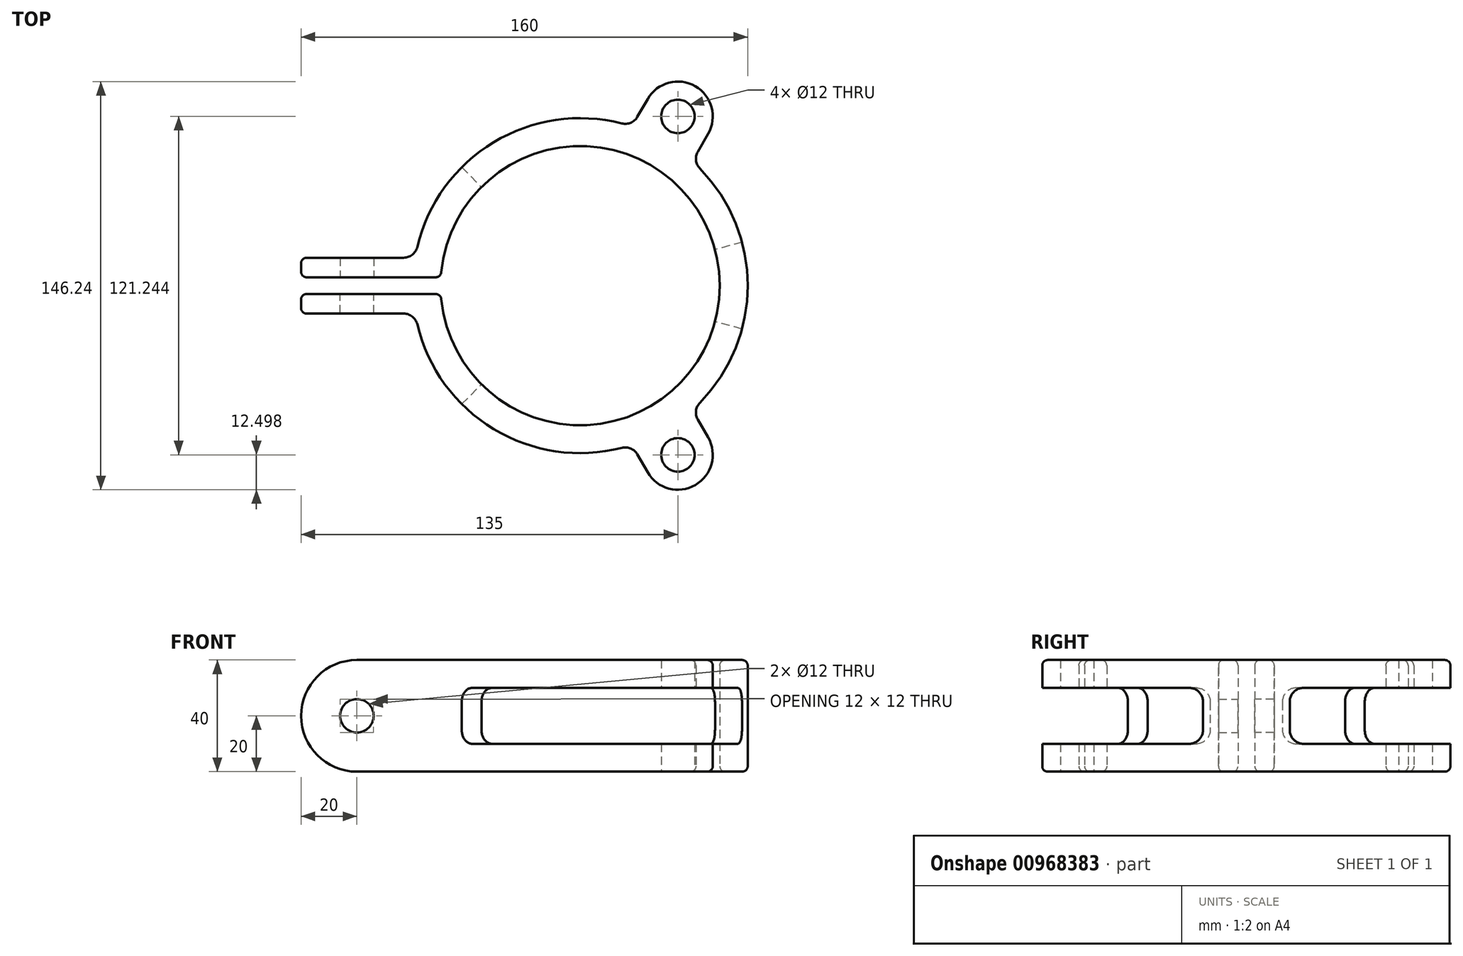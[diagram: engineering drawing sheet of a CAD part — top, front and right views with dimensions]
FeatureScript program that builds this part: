
annotation { "Feature Type Name" : "Feature", "Feature Type Description" : "" }
export const myFeature = defineFeature(function(context is Context, id is Id, definition is map)
    precondition{}
    {
        {
            var Q0;
            Q0=qCreatedBy(makeId("Top.planeOp"),FACE);
            var sketch = newSketch(context, id + "F0", { "sketchPlane" : qUnion([Q0])});
            skArc(sketch, "E0", {"start": v(50, 0) * mm, "mid": v(2.4, 49.94) * mm, "end": v(-49.77, 4.8) * mm});
            skArc(sketch, "E1", {"start": v(14.9, 58.12) * mm, "mid": v(-31.03, 51.36) * mm, "end": v(-58.38, 13.85) * mm});
            skLineSegment(sketch, "E2", {"start": v(-51.76, 3) * mm, "end": v(-100, 3) * mm});
            skLineSegment(sketch, "E3", {"start": v(-100, 3) * mm, "end": v(-100, 10) * mm});
            skLineSegment(sketch, "E4", {"start": v(-100, 10) * mm, "end": v(-63.25, 10) * mm});
            skLineSegment(sketch, "E5", {"start": v(50, 0) * mm, "end": v(60, 0) * mm});
            skArc(sketch, "E6", {"start": v(45.22, 53.43) * mm, "mid": v(41.25, 71.45) * mm, "end": v(23.66, 65.88) * mm});
            skCircle(sketch, "E7", {"center": v(35, 60.62) * mm, "radius": 6 * mm});
            skLineSegment(sketch, "E8", {"start": v(35, 60.62) * mm, "end": v(0, 0) * mm, "construction": true});
            skArc(sketch, "E9", {"start": v(70, 0) * mm, "mid": v(0, 70) * mm, "end": v(-70, 0) * mm, "construction": true});
            skLineSegment(sketch, "E10", {"start": v(24.17, 66.87) * mm, "end": v(20.47, 60.46) * mm});
            skLineSegment(sketch, "E11", {"start": v(45.83, 54.37) * mm, "end": v(42.13, 47.96) * mm});
            skPoint(sketch, "E12.newPointA", {"position": v(60, 0) * mm});
            skArc(sketch, "E12.filletArc", {"start": v(14.9, 58.12) * mm, "mid": v(18.08, 58.35) * mm, "end": v(20.47, 60.46) * mm});
            skArc(sketch, "E13", {"start": v(60, 0) * mm, "mid": v(55.56, 22.66) * mm, "end": v(42.88, 41.97) * mm});
            skArc(sketch, "E14.filletArc", {"start": v(42.13, 47.96) * mm, "mid": v(41.5, 44.84) * mm, "end": v(42.88, 41.97) * mm});
            skPoint(sketch, "E15.visualSharp", {"position": v(-59.16, 10) * mm});
            skArc(sketch, "E15.filletArc", {"start": v(-63.25, 10) * mm, "mid": v(-60.14, 11.08) * mm, "end": v(-58.38, 13.85) * mm});
            skPoint(sketch, "E16.visualSharp", {"position": v(-49.9, 3) * mm});
            skArc(sketch, "E16.filletArc", {"start": v(-51.76, 3) * mm, "mid": v(-50.41, 3.52) * mm, "end": v(-49.77, 4.8) * mm});
            skPoint(sketch, "E17.visualSharp", {"position": v(-100, 10) * mm});
            skPoint(sketch, "E18.visualSharp", {"position": v(-100, 3) * mm});
            skSolve(sketch);
        }
        {
            var Q0;
            Q0=makeQuery(id+"F0.imprint","IMPRINT",FACE,{"disambiguationData":[TD([[makeQuery(id+"F0.imprint","IMPRINT",EDGE,{"derivedFrom":sQuery(id+"F0.wireOp",EDGE,"E0")}),-1.0]])]});
            extrude(context, id + "F1", {"entities" : qUnion([Q0]), "depth" : 40 * mm, "offsetDistance" : 25 * mm, "symmetric" : true});
        }
        {
            var Q0;
            Q0=makeQuery(id+"F1.opExtrude","CAP_EDGE",EDGE,{"disambiguationData":[OSD([sQuery(id+"F0.wireOp",EDGE,"E3")])],"isStart":false});
            var Q1;
            Q1=makeQuery(id+"F1.opExtrude","CAP_EDGE",EDGE,{"disambiguationData":[OSD([sQuery(id+"F0.wireOp",EDGE,"E3")])],"isStart":true});
            fillet(context, id + "F2", {"entities" : qUnion([Q0, Q1]), "radius" : 20 * mm, "tangentPropagation" : true, "allowEdgeOverflow" : false});
        }
        {
            var Q0;
            Q0=qCreatedBy(makeId("Front.planeOp"),FACE);
            var sketch = newSketch(context, id + "F3", { "sketchPlane" : qUnion([Q0])});
            skCircle(sketch, "E19", {"center": v(-80, 0) * mm, "radius": 6 * mm});
            skSolve(sketch);
        }
        {
            var Q0;
            Q0=makeQuery(id+"F3.imprint","IMPRINT",FACE,{"disambiguationData":[TD([[makeQuery(id+"F3.imprint","IMPRINT",EDGE,{"derivedFrom":sQuery(id+"F3.wireOp",EDGE,"E19")}),1.0]])]});
            extrude(context, id + "F4", {"entities" : qUnion([Q0]), "operationType" : NewBodyOperationType.REMOVE, "endBound" : BoundingType.THROUGH_ALL, "oppositeDirection" : true, "depth" : 25 * mm, "offsetDistance" : 25 * mm});
        }
        {
            var Q0;
            Q0=qCreatedBy(makeId("Top.planeOp"),FACE);
            var sketch = newSketch(context, id + "F5", { "sketchPlane" : qUnion([Q0])});
            skArc(sketch, "E20.0", {"start": v(14.9, 58.12) * mm, "mid": v(-15.84, 57.87) * mm, "end": v(-42.43, 42.43) * mm});
            skArc(sketch, "E20.1", {"start": v(48.3, 12.94) * mm, "mid": v(12.94, 48.3) * mm, "end": v(-35.36, 35.36) * mm});
            skLineSegment(sketch, "E21", {"start": v(-42.43, 42.43) * mm, "end": v(-35.36, 35.36) * mm});
            skPoint(sketch, "E22.orphan", {"position": v(14.9, 58.12) * mm});
            skLineSegment(sketch, "E23", {"start": v(57.96, 15.53) * mm, "end": v(48.3, 12.94) * mm});
            skPoint(sketch, "E24.orphan", {"position": v(50, 0) * mm});
            skPoint(sketch, "E25.orphan", {"position": v(-49.77, 4.8) * mm});
            skPoint(sketch, "E26.orphan", {"position": v(-58.38, 13.85) * mm});
            skArc(sketch, "E27.0", {"start": v(57.96, 15.53) * mm, "mid": v(52.12, 29.72) * mm, "end": v(42.88, 41.97) * mm});
            skArc(sketch, "E27.1", {"start": v(42.13, 47.96) * mm, "mid": v(41.5, 44.84) * mm, "end": v(42.88, 41.97) * mm});
            skLineSegment(sketch, "E27.2", {"start": v(45.83, 54.37) * mm, "end": v(42.13, 47.96) * mm});
            skArc(sketch, "E27.3", {"start": v(45.22, 53.43) * mm, "mid": v(41.25, 71.45) * mm, "end": v(23.66, 65.88) * mm});
            skLineSegment(sketch, "E27.4", {"start": v(24.17, 66.87) * mm, "end": v(20.47, 60.46) * mm});
            skArc(sketch, "E27.5", {"start": v(14.9, 58.12) * mm, "mid": v(18.08, 58.35) * mm, "end": v(20.47, 60.46) * mm});
            skPoint(sketch, "E28.orphan", {"position": v(60, 0) * mm});
            skSolve(sketch);
        }
        {
            var Q0;
            Q0 = qSketchRegion(id + "F5", true);
            extrude(context, id + "F6", {"entities" : qUnion([Q0]), "operationType" : NewBodyOperationType.REMOVE, "depth" : 20 * mm, "offsetDistance" : 25 * mm, "symmetric" : true});
        }
        {
            var Q0;
            Q0=makeQuery(id+"F6.boolean.opBoolean","COPY",EDGE,{"derivedFrom":makeQuery(id+"F6.opExtrude","CAP_EDGE",EDGE,{"disambiguationData":[OSD([sQuery(id+"F5.wireOp",EDGE,"E21")])],"isStart":true})});
            var Q1;
            Q1=makeQuery(id+"F6.boolean.opBoolean","COPY",EDGE,{"derivedFrom":makeQuery(id+"F6.opExtrude","CAP_EDGE",EDGE,{"disambiguationData":[OSD([sQuery(id+"F5.wireOp",EDGE,"E21")])],"isStart":false})});
            var Q2;
            Q2=makeQuery(id+"F6.boolean.opBoolean","COPY",EDGE,{"derivedFrom":makeQuery(id+"F6.opExtrude","CAP_EDGE",EDGE,{"disambiguationData":[OSD([sQuery(id+"F5.wireOp",EDGE,"E23")])],"isStart":false})});
            var Q3;
            Q3=makeQuery(id+"F6.boolean.opBoolean","COPY",EDGE,{"derivedFrom":makeQuery(id+"F6.opExtrude","CAP_EDGE",EDGE,{"disambiguationData":[OSD([sQuery(id+"F5.wireOp",EDGE,"E23")])],"isStart":true})});
            fillet(context, id + "F7", {"entities" : qUnion([Q0, Q1, Q2, Q3]), "radius" : 5 * mm, "tangentPropagation" : true, "allowEdgeOverflow" : false});
        }
        {
            var Q0;
            Q0=makeQuery(id+"F6.boolean.opBoolean","COPY",EDGE,{"derivedFrom":makeQuery(id+"F6.opExtrude","CAP_EDGE",EDGE,{"disambiguationData":[OSD([sQuery(id+"F5.wireOp",EDGE,"E20.0")])],"isStart":false})});
            var Q1;
            Q1=makeQuery(id+"F1.opExtrude","CAP_EDGE",EDGE,{"disambiguationData":[OSD([sQuery(id+"F0.wireOp",EDGE,"E1")])],"isStart":false});
            var Q2;
            Q2=makeQuery(id+"F1.opExtrude","CAP_EDGE",EDGE,{"disambiguationData":[OSD([sQuery(id+"F0.wireOp",EDGE,"E0")])],"isStart":false});
            fillet(context, id + "F8", {"entities" : qUnion([Q0, Q1, Q2]), "radius" : 2 * mm, "tangentPropagation" : true, "allowEdgeOverflow" : false});
        }
        {
            var Q0;
            Q0=makeQuery(id+"F1.opExtrude","SWEPT_BODY",BODY,{"disambiguationData":[OSD([sQuery(id+"F0.wireOp",EDGE,"E0"),sQuery(id+"F0.wireOp",EDGE,"E1"),sQuery(id+"F0.wireOp",EDGE,"E2"),sQuery(id+"F0.wireOp",EDGE,"E3"),sQuery(id+"F0.wireOp",EDGE,"E4"),sQuery(id+"F0.wireOp",EDGE,"E5"),sQuery(id+"F0.wireOp",EDGE,"E6"),sQuery(id+"F0.wireOp",EDGE,"E7"),sQuery(id+"F0.wireOp",EDGE,"E10"),sQuery(id+"F0.wireOp",EDGE,"E11"),sQuery(id+"F0.wireOp",EDGE,"E12.filletArc"),sQuery(id+"F0.wireOp",EDGE,"E13"),sQuery(id+"F0.wireOp",EDGE,"E14.filletArc"),sQuery(id+"F0.wireOp",EDGE,"E15.filletArc"),sQuery(id+"F0.wireOp",EDGE,"E16.filletArc")])]});
            var Q1;
            Q1=qCreatedBy(makeId("Front.planeOp"),FACE);
            mirror(context, id + "F9", {"operationType" : NewBodyOperationType.ADD, "entities" : qUnion([Q0]), "mirrorPlane" : qUnion([Q1])});
        }
    });
